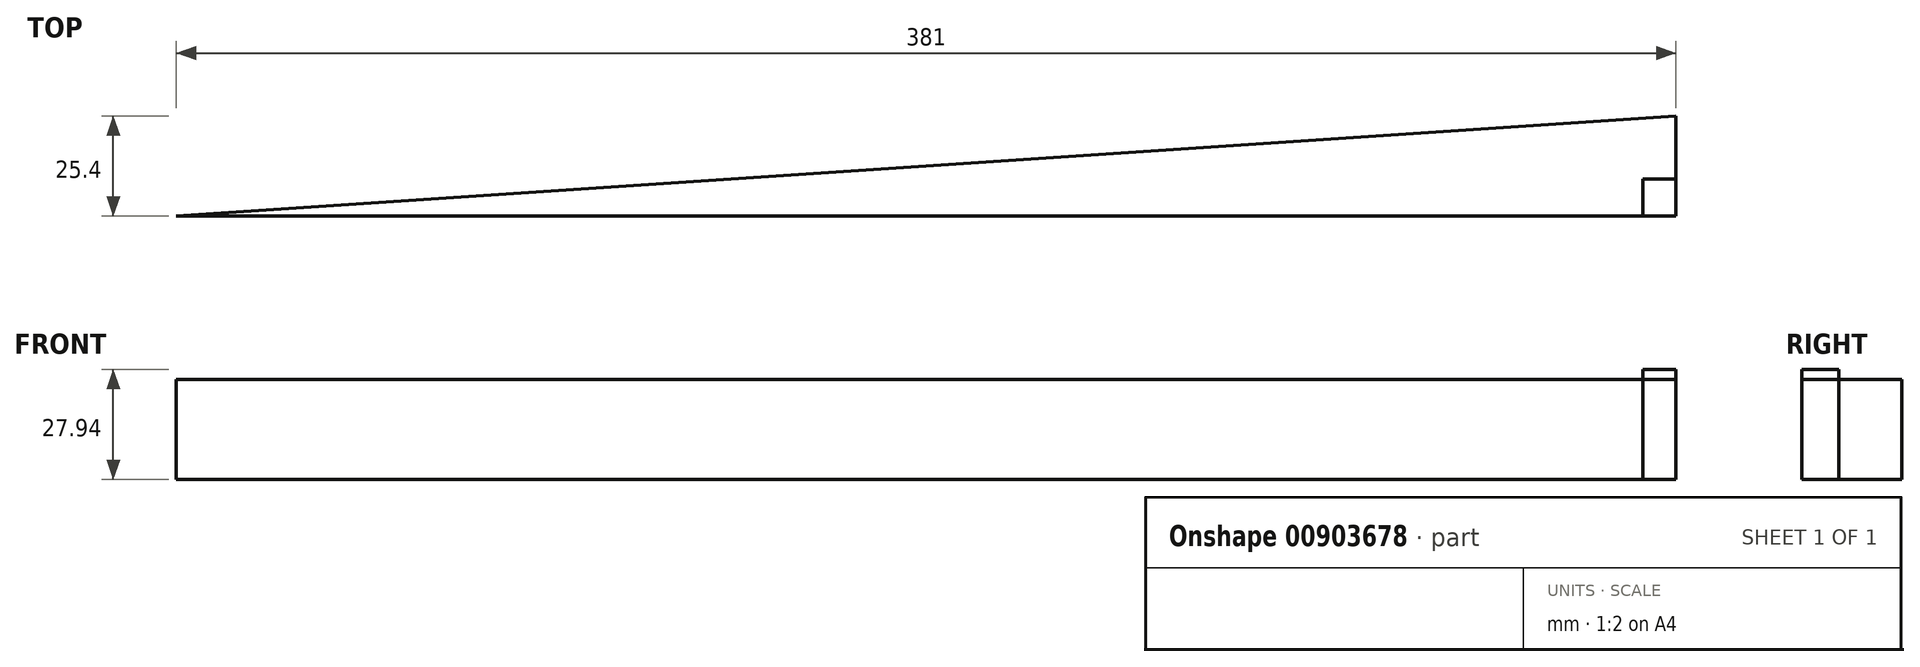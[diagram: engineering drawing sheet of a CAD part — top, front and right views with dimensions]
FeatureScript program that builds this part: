
annotation { "Feature Type Name" : "Feature", "Feature Type Description" : "" }
export const myFeature = defineFeature(function(context is Context, id is Id, definition is map)
    precondition{}
    {
        {
            var Q0;
            Q0=qCreatedBy(makeId("Top.planeOp"),FACE);
            var sketch = newSketch(context, id + "F0", { "sketchPlane" : qUnion([Q0])});
            skLineSegment(sketch, "E0", {"start": v(102.15, -265.9) * mm, "end": v(483.15, -265.9) * mm});
            skLineSegment(sketch, "E1", {"start": v(483.15, -265.9) * mm, "end": v(483.15, -240.5) * mm});
            skLineSegment(sketch, "E2", {"start": v(483.15, -240.5) * mm, "end": v(102.15, -265.9) * mm});
            skLineSegment(sketch, "E3", {"start": v(483.15, -256.55) * mm, "end": v(474.77, -256.55) * mm});
            skLineSegment(sketch, "E4", {"start": v(474.77, -256.55) * mm, "end": v(474.77, -265.9) * mm});
            skSolve(sketch);
        }
        {
            var Q0;
            Q0 = qSketchRegion(id + "F0", true);
            extrude(context, id + "F1", {"entities" : qUnion([Q0]), "depth" : 25.4 * mm, "offsetDistance" : 25.4 * mm});
        }
        {
            var Q0;
            {var subQ4=sQuery(id+"F0.wireOp",EDGE,"E3");Q0=makeQuery(id+"F0.imprint","IMPRINT",FACE,{"disambiguationData":[TD([[makeQuery(id+"F0.imprint","IMPRINT",EDGE,{"derivedFrom":subQ4}),1.0]])]});}
            extrude(context, id + "F2", {"entities" : qUnion([Q0]), "depth" : 27.94 * mm, "offsetDistance" : 25.4 * mm});
        }
    });
